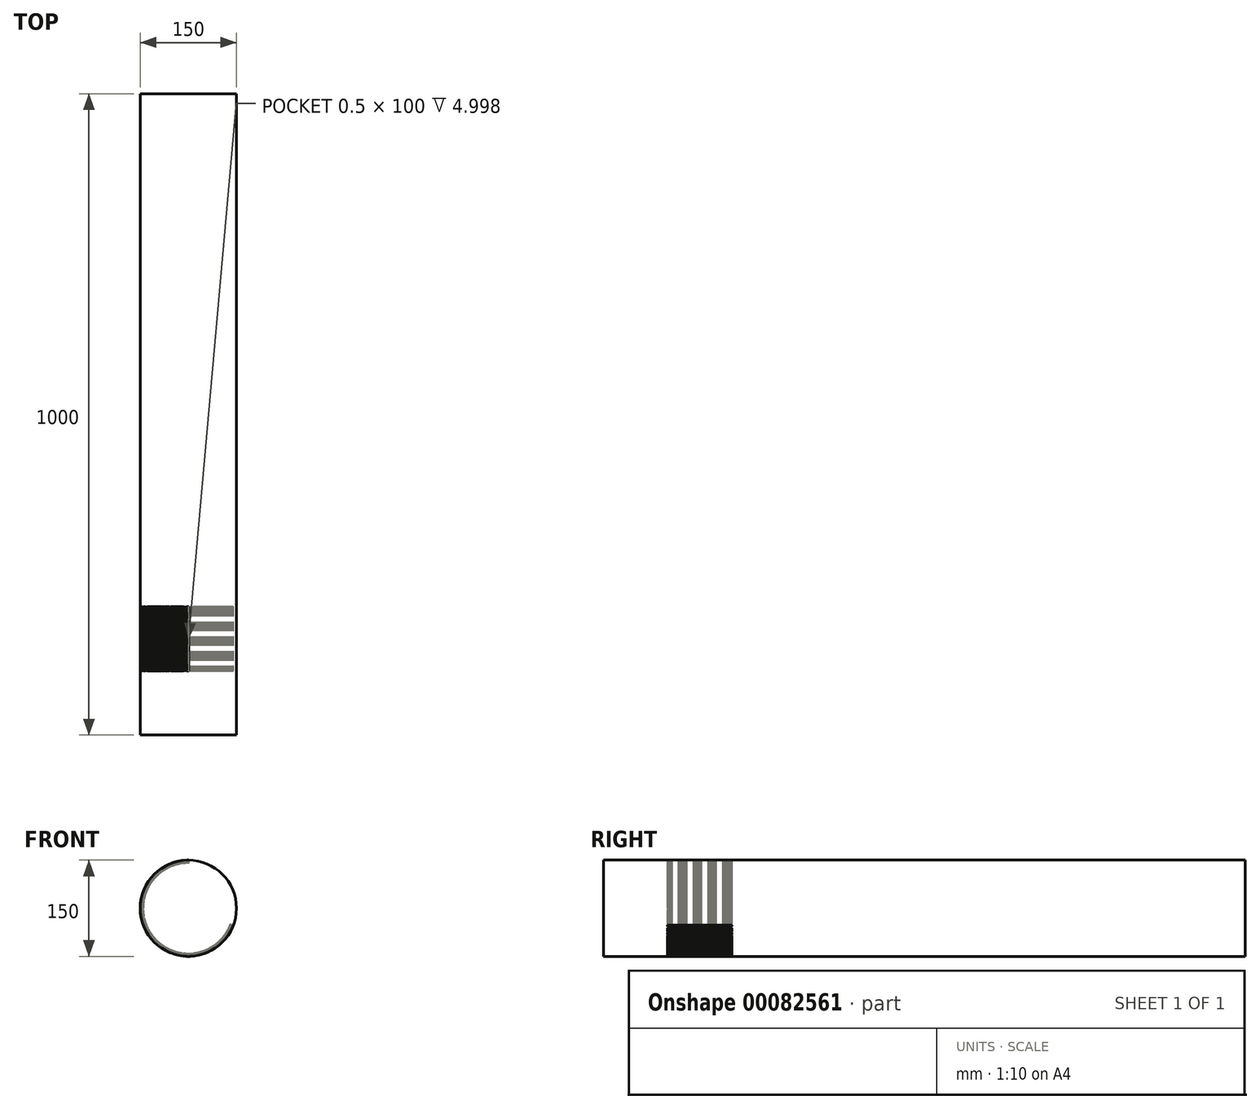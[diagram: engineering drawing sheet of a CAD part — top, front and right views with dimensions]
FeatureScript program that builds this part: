
annotation { "Feature Type Name" : "Feature", "Feature Type Description" : "" }
export const myFeature = defineFeature(function(context is Context, id is Id, definition is map)
    precondition{}
    {
        {
            var Q0;
            Q0=qCreatedBy(makeId("Front.planeOp"),FACE);
            var sketch = newSketch(context, id + "F0", { "sketchPlane" : qUnion([Q0])});
            skCircle(sketch, "E0", {"center": v(0, 0) * mm, "radius": 75 * mm});
            skSolve(sketch);
        }
        {
            var Q0;
            Q0=makeQuery(id+"F0.imprint","IMPRINT",FACE,{"disambiguationData":[TD([[makeQuery(id+"F0.imprint","IMPRINT",EDGE,{"derivedFrom":sQuery(id+"F0.wireOp",EDGE,"E0")}),1.0]])]});
            extrude(context, id + "F1", {"entities" : qUnion([Q0]), "depth" : 1000 * mm});
        }
        {
            var Q0;
            Q0=makeQuery(id+"F1.opExtrude","CAP_FACE",FACE,{"disambiguationData":[OSD([sQuery(id+"F0.wireOp",EDGE,"E0")])],"isStart":false});
            cPlane(context, id + "F2", {"entities" : qUnion([Q0]), "cplaneType" : CPlaneType.OFFSET, "offset" : 100 * mm, "oppositeDirection" : true, "width" : 150 * mm, "height" : 150 * mm});
        }
        {
            var Q0;
            Q0=qCreatedBy(id+"F2.planeOp",FACE);
            var sketch = newSketch(context, id + "F3", { "sketchPlane" : qUnion([Q0])});
            skCircle(sketch, "E1.0", {"center": v(0, 0) * mm, "radius": 75 * mm});
            skLineSegment(sketch, "E2", {"start": v(0, 75) * mm, "end": v(0.5, 75) * mm});
            skLineSegment(sketch, "E3", {"start": v(0.5, 75) * mm, "end": v(0.5, 70) * mm});
            skLineSegment(sketch, "E4", {"start": v(0.5, 70) * mm, "end": v(0, 70) * mm});
            skLineSegment(sketch, "E5", {"start": v(0, 70) * mm, "end": v(0, 75) * mm});
            skSolve(sketch);
        }
        {
            var Q0;
            {var subQ4=sQuery(id+"F3.wireOp",EDGE,"E4");Q0=makeQuery(id+"F3.imprint","IMPRINT",FACE,{"disambiguationData":[TD([[makeQuery(id+"F3.imprint","IMPRINT",EDGE,{"derivedFrom":subQ4}),-1.0]])]});}
            extrude(context, id + "F4", {"entities" : qUnion([Q0]), "operationType" : NewBodyOperationType.REMOVE, "oppositeDirection" : true, "depth" : 100 * mm});
        }
        {
            var Q0;
            Q0=makeQuery(id+"F4.boolean.opBoolean","COPY",FACE,{"derivedFrom":makeQuery(id+"F4.opExtrude","SWEPT_FACE",FACE,{"disambiguationData":[OSD([sQuery(id+"F3.wireOp",EDGE,"E3")])]})});
            var Q1;
            Q1=makeQuery(id+"F4.boolean.opBoolean","COPY",FACE,{"derivedFrom":makeQuery(id+"F4.opExtrude","CAP_FACE",FACE,{"disambiguationData":[OSD([sQuery(id+"F3.wireOp",EDGE,"E1.0"),sQuery(id+"F3.wireOp",EDGE,"E3"),sQuery(id+"F3.wireOp",EDGE,"E4"),sQuery(id+"F3.wireOp",EDGE,"E5")])],"isStart":false})});
            var Q2;
            Q2=makeQuery(id+"F4.boolean.opBoolean","COPY",FACE,{"derivedFrom":makeQuery(id+"F4.opExtrude","SWEPT_FACE",FACE,{"disambiguationData":[OSD([sQuery(id+"F3.wireOp",EDGE,"E5")])]})});
            var Q3;
            Q3=makeQuery(id+"F4.boolean.opBoolean","COPY",FACE,{"derivedFrom":makeQuery(id+"F4.opExtrude","SWEPT_FACE",FACE,{"disambiguationData":[OSD([sQuery(id+"F3.wireOp",EDGE,"E4")])]})});
            var Q4;
            Q4=makeQuery(id+"F4.boolean.opBoolean","COPY",FACE,{"derivedFrom":makeQuery(id+"F4.opExtrude","CAP_FACE",FACE,{"disambiguationData":[OSD([sQuery(id+"F3.wireOp",EDGE,"E1.0"),sQuery(id+"F3.wireOp",EDGE,"E3"),sQuery(id+"F3.wireOp",EDGE,"E4"),sQuery(id+"F3.wireOp",EDGE,"E5")])],"isStart":true})});
            var Q5;
            Q5=makeQuery(id+"F1.opExtrude","CAP_EDGE",EDGE,{"disambiguationData":[OSD([sQuery(id+"F0.wireOp",EDGE,"E0")])],"isStart":false});
            circularPattern(context, id + "F5", {"faces" : qUnion([Q0, Q1, Q2, Q3, Q4]), "axis" : qUnion([Q5]), "angle" : 0.5 * degree, "instanceCount" : 500, "patternType" : PatternType.FACE});
        }
    });
